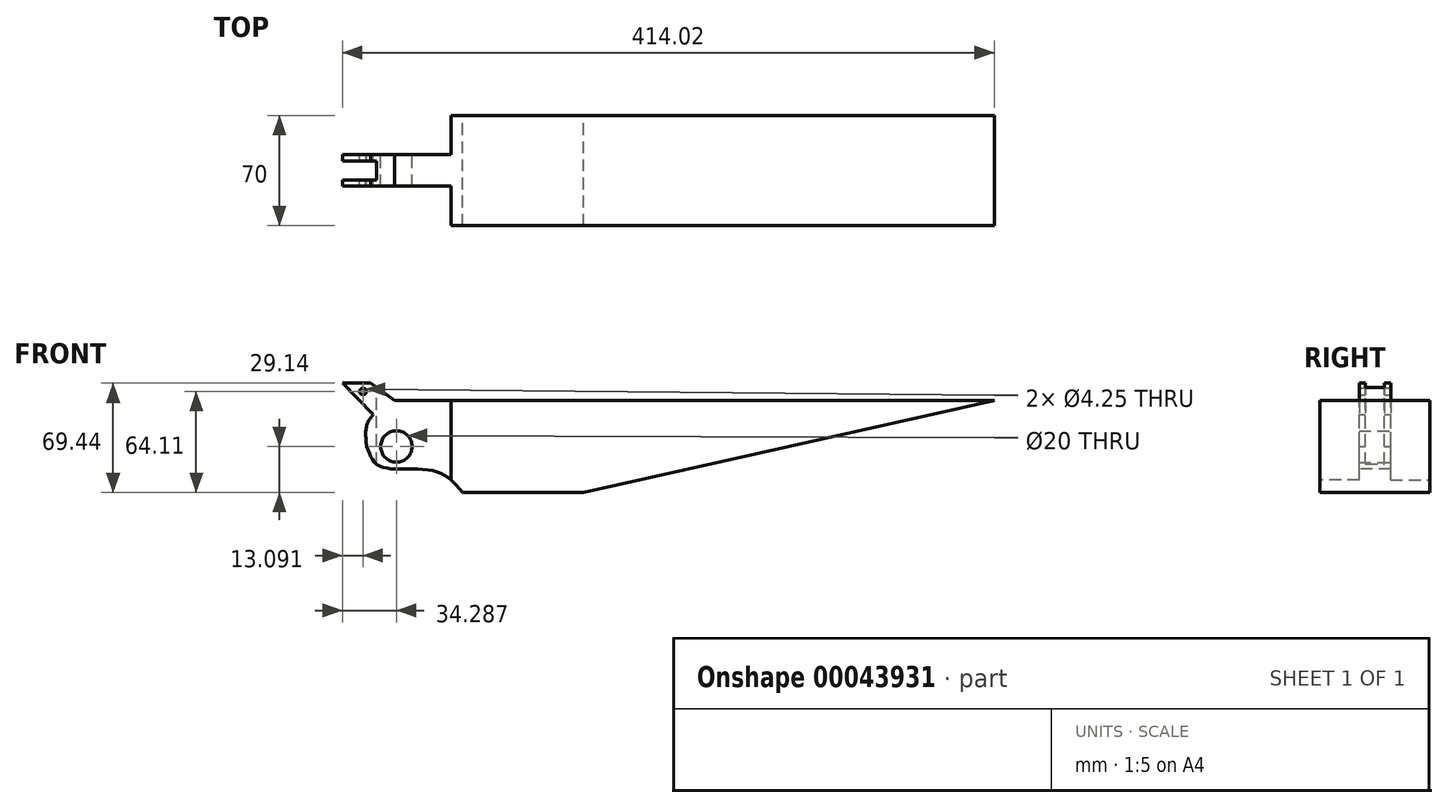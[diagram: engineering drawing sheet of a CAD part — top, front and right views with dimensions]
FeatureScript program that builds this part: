
annotation { "Feature Type Name" : "Feature", "Feature Type Description" : "" }
export const myFeature = defineFeature(function(context is Context, id is Id, definition is map)
    precondition{}
    {
        {
            var Q0;
            Q0=qCreatedBy(makeId("Front.planeOp"),FACE);
            var sketch = newSketch(context, id + "F0", { "sketchPlane" : qUnion([Q0])});
            skLineSegment(sketch, "E0.rect.bottom", {"start": v(60, 29.14) * mm, "end": v(-60, 29.14) * mm, "construction": true});
            skLineSegment(sketch, "E0.rect.left", {"start": v(60, 29.14) * mm, "end": v(60, -29.14) * mm, "construction": true});
            skPoint(sketch, "E0.rect.middle", {"position": v(0, 0) * mm});
            skLineSegment(sketch, "E1", {"start": v(-60, 29.14) * mm, "end": v(60, 29.14) * mm});
            skLineSegment(sketch, "E2", {"start": v(60, 29.14) * mm, "end": v(60, -29.14) * mm});
            skLineSegment(sketch, "E3", {"start": v(60, -29.14) * mm, "end": v(-16.67, -29.14) * mm});
            skLineSegment(sketch, "E4", {"start": v(60, 29.14) * mm, "end": v(321, 29.14) * mm});
            skLineSegment(sketch, "E5", {"start": v(321, 29.14) * mm, "end": v(60, -29.14) * mm});
            skLineSegment(sketch, "E6", {"start": v(-60, 29.14) * mm, "end": v(-75.05, 40.3) * mm});
            skCircle(sketch, "E7", {"center": v(-58.73, 0) * mm, "radius": 10 * mm});
            skCircle(sketch, "E8", {"center": v(-79.93, 34.97) * mm, "radius": 2.12 * mm});
            skLineSegment(sketch, "E9", {"start": v(-75.05, 40.3) * mm, "end": v(-93.02, 40.3) * mm});
            skLineSegment(sketch, "E10", {"start": v(-93.02, 40.3) * mm, "end": v(-73.5, 20.44) * mm});
            skFitSpline(sketch, "E11", {"points": [v(-16.67, -29.14) * mm, v(-35.18, -15.42) * mm, v(-68.8, -12.69) * mm, v(-77.64, 0) * mm], "startDerivative": vector(-46.1, 56.12) * mm, "endDerivative": vector(-24.62, 62.58) * mm});
            skFitSpline(sketch, "E12", {"points": [v(-77.64, 0) * mm, v(-77.64, 13.17) * mm, v(-73.5, 20.44) * mm], "startDerivative": vector(-2.6, 25.69) * mm, "endDerivative": vector(11.4, 14.78) * mm});
            skSolve(sketch);
        }
        {
            var Q0;
            Q0 = qSketchRegion(id + "F0", true);
            extrude(context, id + "F1", {"entities" : qUnion([Q0]), "depth" : 70 * mm});
        }
        {
            var Q0;
            Q0=qCreatedBy(makeId("Top.planeOp"),FACE);
            var sketch = newSketch(context, id + "F2", { "sketchPlane" : qUnion([Q0])});
            skLineSegment(sketch, "E13.0", {"start": v(-60, 0) * mm, "end": v(321, 0) * mm, "construction": true});
            skLineSegment(sketch, "E14.bottom", {"start": v(-120.28, -25) * mm, "end": v(-23.97, -25) * mm});
            skLineSegment(sketch, "E14.top", {"start": v(-122.66, -45) * mm, "end": v(-23.97, -45) * mm});
            skLineSegment(sketch, "E15", {"start": v(0, 0) * mm, "end": v(0, -70) * mm, "construction": true});
            skLineSegment(sketch, "E16", {"start": v(-120.28, -25) * mm, "end": v(-120.28, 0) * mm});
            skLineSegment(sketch, "E17", {"start": v(-120.28, 0) * mm, "end": v(-60, 0) * mm});
            skLineSegment(sketch, "E18", {"start": v(-23.97, -25) * mm, "end": v(-23.97, 0) * mm});
            skLineSegment(sketch, "E19", {"start": v(-122.66, -45) * mm, "end": v(-122.66, -72.71) * mm});
            skLineSegment(sketch, "E20", {"start": v(-122.66, -72.71) * mm, "end": v(-24, -72.71) * mm});
            skLineSegment(sketch, "E21", {"start": v(-24, -72.71) * mm, "end": v(-23.97, -45) * mm});
            skLineSegment(sketch, "E22", {"start": v(-60, 0) * mm, "end": v(-23.97, 0) * mm});
            skLineSegment(sketch, "E23.bottom", {"start": v(-95.19, -29) * mm, "end": v(-71.4, -29) * mm});
            skLineSegment(sketch, "E23.top", {"start": v(-95.19, -41) * mm, "end": v(-71.4, -41) * mm});
            skLineSegment(sketch, "E23.left", {"start": v(-95.19, -29) * mm, "end": v(-95.19, -41) * mm});
            skLineSegment(sketch, "E23.right", {"start": v(-71.4, -29) * mm, "end": v(-71.4, -41) * mm});
            skSolve(sketch);
        }
        {
            var Q0;
            Q0 = qSketchRegion(id + "F2", true);
            extrude(context, id + "F3", {"entities" : qUnion([Q0]), "operationType" : NewBodyOperationType.REMOVE, "endBound" : BoundingType.SYMMETRIC, "oppositeDirection" : true, "depth" : 100 * mm});
        }
    });
